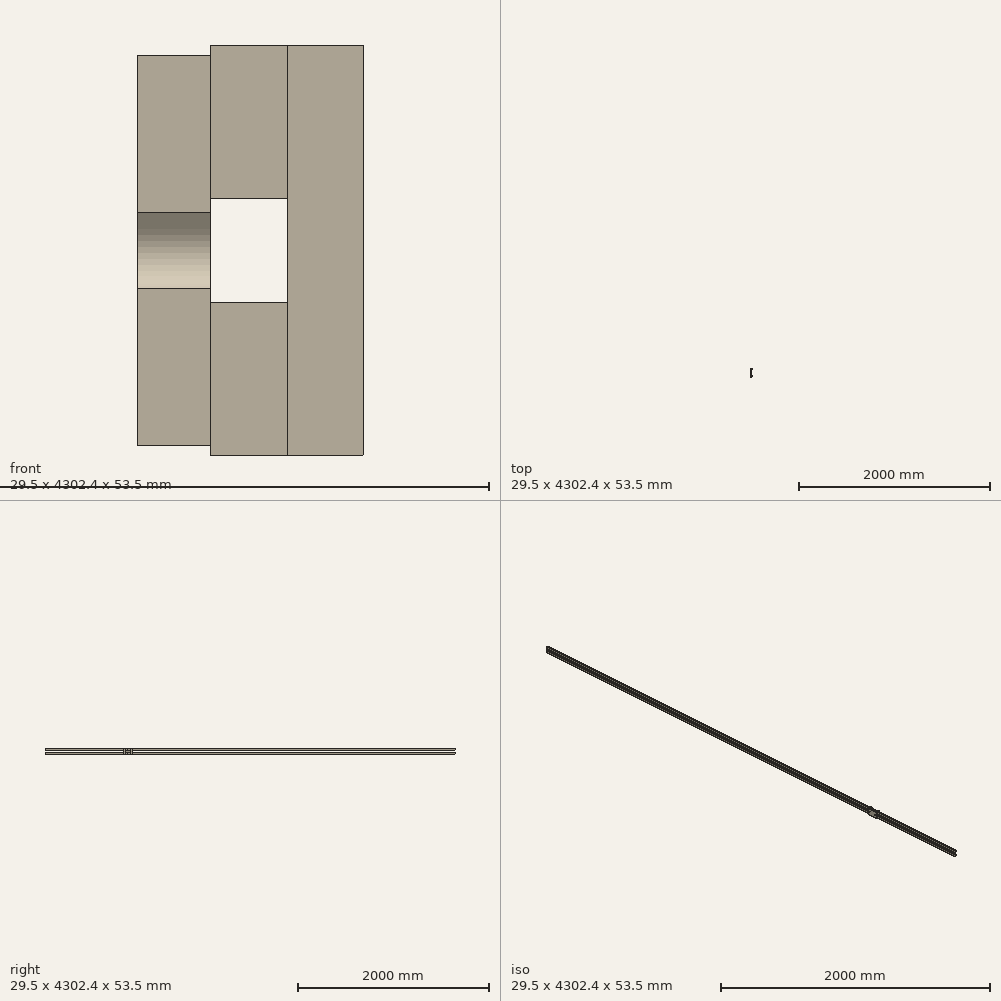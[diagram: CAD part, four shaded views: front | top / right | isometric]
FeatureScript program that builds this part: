
annotation { "Feature Type Name" : "Feature", "Feature Type Description" : "" }
export const myFeature = defineFeature(function(context is Context, id is Id, definition is map)
    precondition{}
    {
        {
            var Q0;
            Q0=qCreatedBy(makeId("Front.planeOp"),FACE);
            var sketch = newSketch(context, id + "F0", { "sketchPlane" : qUnion([Q0])});
            skLineSegment(sketch, "E0.bottom", {"start": v(-47.15, 37.14) * mm, "end": v(-37.15, 37.14) * mm});
            skLineSegment(sketch, "E0.top", {"start": v(-47.15, 17.14) * mm, "end": v(-37.15, 17.14) * mm});
            skLineSegment(sketch, "E0.left", {"start": v(-47.15, 37.14) * mm, "end": v(-47.15, 17.14) * mm});
            skLineSegment(sketch, "E0.right", {"start": v(-37.15, 37.14) * mm, "end": v(-37.15, 17.14) * mm});
            skLineSegment(sketch, "E1.bottom", {"start": v(-47.15, 3.67) * mm, "end": v(-37.15, 3.67) * mm});
            skLineSegment(sketch, "E1.top", {"start": v(-47.15, -16.33) * mm, "end": v(-37.15, -16.33) * mm});
            skLineSegment(sketch, "E1.left", {"start": v(-47.15, 3.67) * mm, "end": v(-47.15, -16.33) * mm});
            skLineSegment(sketch, "E1.right", {"start": v(-37.15, 3.67) * mm, "end": v(-37.15, -16.33) * mm});
            skPoint(sketch, "E2.startSnap0", {"position": v(-42.15, 37.14) * mm});
            skPoint(sketch, "E2.startSnap1", {"position": v(-47.15, 27.14) * mm});
            skPoint(sketch, "E2.endSnap0", {"position": v(-47.15, -6.33) * mm});
            skPoint(sketch, "E2.endSnap1", {"position": v(-42.15, 3.67) * mm});
            skSolve(sketch);
        }
        {
            var Q0;
            Q0=makeQuery(id+"F0.imprint","IMPRINT",FACE,{"disambiguationData":[TD([[makeQuery(id+"F0.imprint","IMPRINT",EDGE,{"derivedFrom":sQuery(id+"F0.wireOp",EDGE,"E0.bottom")}),-1.0]])]});
            var Q1;
            Q1=makeQuery(id+"F0.imprint","IMPRINT",FACE,{"disambiguationData":[TD([[makeQuery(id+"F0.imprint","IMPRINT",EDGE,{"derivedFrom":sQuery(id+"F0.wireOp",EDGE,"E1.bottom")}),-1.0]])]});
            extrude(context, id + "F1", {"entities" : qUnion([Q0, Q1]), "depth" : 4302.45 * mm});
        }
        {
            var Q0;
            Q0=makeQuery(id+"F1.opExtrude","SWEPT_FACE",FACE,{"disambiguationData":[OSD([sQuery(id+"F0.wireOp",EDGE,"E0.left")])]});
            var sketch = newSketch(context, id + "F2", { "sketchPlane" : qUnion([Q0])});
            skLineSegment(sketch, "E3.0.0", {"start": v(0, 3.67) * mm, "end": v(0, -16.33) * mm});
            skLineSegment(sketch, "E3.0.1", {"start": v(0, -16.33) * mm, "end": v(4302.45, -16.33) * mm});
            skLineSegment(sketch, "E3.0.2", {"start": v(4302.45, -16.33) * mm, "end": v(4302.45, 3.67) * mm});
            skLineSegment(sketch, "E3.0.3", {"start": v(4302.45, 3.67) * mm, "end": v(0, 3.67) * mm});
            skLineSegment(sketch, "E4", {"start": v(3483.33, 10.4) * mm, "end": v(3483.33, 35.8) * mm});
            skLineSegment(sketch, "E5", {"start": v(3483.33, 35.8) * mm, "end": v(3483.33, 10.4) * mm});
            skLineSegment(sketch, "E6", {"start": v(3483.33, 10.4) * mm, "end": v(3483.33, -15) * mm});
            skSolve(sketch);
        }
        {
            var Q0;
            Q0=sQuery(id+"F2.wireOp",EDGE,"E6");
            var Q1;
            Q1=sQuery(id+"F2.wireOp",EDGE,"E5");
            extrude(context, id + "F3", {"bodyType" : ToolBodyType.SURFACE, "surfaceEntities" : qUnion([Q0, Q1]), "depth" : 9.53 * mm, "offsetDistance" : 25 * mm});
        }
        {
            var Q0;
            Q0=makeQuery(id+"F3.opExtrude","SWEPT_FACE",FACE,{"disambiguationData":[OSD([sQuery(id+"F2.wireOp",EDGE,"E5"),sQuery(id+"F2.wireOp",EDGE,"E6")])]});
            extrude(context, id + "F4", {"entities" : qUnion([Q0]), "depth" : 90 * mm, "offsetDistance" : 25 * mm});
        }
        {
            var Q0;
            {var subQ0=sQuery(id+"F2.wireOp",EDGE,"E6");var subQ1=sQuery(id+"F2.wireOp",EDGE,"E5");Q0=makeQuery(id+"F4.opExtrude","SWEPT_FACE",FACE,{"disambiguationData":[OSD([subQ1,subQ0]),TDD([makeQuery(id+"F3.opExtrude","CAP_EDGE",EDGE,{"disambiguationData":[OSD([subQ1,subQ0])],"isStart":false})])]});}
            var sketch = newSketch(context, id + "F5", { "sketchPlane" : qUnion([Q0])});
            skLineSegment(sketch, "E7", {"start": v(3468.33, 5.4) * mm, "end": v(3483.33, 5.4) * mm});
            skLineSegment(sketch, "E8.MirrorCS", {"start": v(3468.33, 15.4) * mm, "end": v(3483.33, 15.4) * mm});
            skLineSegment(sketch, "E9", {"start": v(3468.33, 5.4) * mm, "end": v(3473.33, 5.4) * mm});
            skArc(sketch, "E10", {"start": v(3468.33, 15.4) * mm, "mid": v(3463.33, 10.4) * mm, "end": v(3468.33, 5.4) * mm});
            skSolve(sketch);
        }
        {
            var Q0;
            Q0=makeQuery(id+"F1.opExtrude","SWEPT_FACE",FACE,{"disambiguationData":[OSD([sQuery(id+"F0.wireOp",EDGE,"E1.right")])]});
            var sketch = newSketch(context, id + "F6", { "sketchPlane" : qUnion([Q0])});
            skLineSegment(sketch, "E11.0.0", {"start": v(-3483.33, 35.8) * mm, "end": v(-3483.33, 15.4) * mm});
            skLineSegment(sketch, "E11.0.4", {"start": v(-3483.33, 5.4) * mm, "end": v(-3483.33, -15) * mm});
            skLineSegment(sketch, "E11.0.6", {"start": v(-3393.33, -15) * mm, "end": v(-3393.33, 5.4) * mm});
            skLineSegment(sketch, "E11.0.10", {"start": v(-3393.33, 15.4) * mm, "end": v(-3393.33, 35.8) * mm});
            skLineSegment(sketch, "E12.0.1", {"start": v(0, 37.14) * mm, "end": v(-4302.45, 37.14) * mm});
            skLineSegment(sketch, "E13", {"start": v(-3483.33, 35.8) * mm, "end": v(-3483.33, 37.14) * mm});
            skLineSegment(sketch, "E14", {"start": v(-3483.33, 15.4) * mm, "end": v(-3483.33, 5.4) * mm});
            skLineSegment(sketch, "E15", {"start": v(-3483.33, -15) * mm, "end": v(-3483.33, -16.33) * mm});
            skLineSegment(sketch, "E16", {"start": v(-3483.33, -16.33) * mm, "end": v(-3463.33, -16.33) * mm});
            skLineSegment(sketch, "E17", {"start": v(-3463.33, -16.33) * mm, "end": v(-3463.33, 37.14) * mm});
            skLineSegment(sketch, "E18", {"start": v(-3463.33, 37.14) * mm, "end": v(-3483.33, 37.14) * mm});
            skLineSegment(sketch, "E19", {"start": v(-3393.33, 15.4) * mm, "end": v(-3393.33, 5.4) * mm});
            skLineSegment(sketch, "E20", {"start": v(-3393.33, 35.8) * mm, "end": v(-3393.33, 37.14) * mm});
            skLineSegment(sketch, "E21", {"start": v(-3393.33, 37.14) * mm, "end": v(-3413.33, 37.14) * mm});
            skLineSegment(sketch, "E22", {"start": v(-3413.33, 37.14) * mm, "end": v(-3413.33, -16.33) * mm});
            skLineSegment(sketch, "E23", {"start": v(-3413.33, -16.33) * mm, "end": v(-3393.33, -16.33) * mm});
            skLineSegment(sketch, "E24", {"start": v(-3393.33, -16.33) * mm, "end": v(-3393.33, -15) * mm});
            skSolve(sketch);
        }
        {
            var Q0;
            Q0=makeQuery(id+"F6.imprint","IMPRINT",FACE,{"disambiguationData":[TD([[makeQuery(id+"F6.imprint","IMPRINT",EDGE,{"derivedFrom":sQuery(id+"F6.wireOp",EDGE,"E11.0.0")}),1.0]])]});
            var Q1;
            {var subQ5=sQuery(id+"F6.wireOp",EDGE,"E15");Q1=makeQuery(id+"F6.imprint","IMPRINT",FACE,{"disambiguationData":[TD([[makeQuery(id+"F6.imprint","IMPRINT",EDGE,{"derivedFrom":subQ5}),1.0]])]});}
            var Q2;
            Q2=makeQuery(id+"F6.imprint","IMPRINT",FACE,{"disambiguationData":[TD([[makeQuery(id+"F6.imprint","IMPRINT",EDGE,{"derivedFrom":sQuery(id+"F6.wireOp",EDGE,"E11.0.10")}),1.0]])]});
            var Q3;
            {var subQ1=sQuery(id+"F6.wireOp",EDGE,"E23");Q3=makeQuery(id+"F6.imprint","IMPRINT",FACE,{"disambiguationData":[TD([[makeQuery(id+"F6.imprint","IMPRINT",EDGE,{"derivedFrom":subQ1}),1.0]])]});}
            extrude(context, id + "F7", {"entities" : qUnion([Q0, Q1, Q2, Q3]), "depth" : 10 * mm, "offsetDistance" : 25 * mm});
        }
        {
            var Q0;
            Q0=makeQuery(id+"F1.opExtrude","SWEPT_FACE",FACE,{"disambiguationData":[OSD([sQuery(id+"F0.wireOp",EDGE,"E0.bottom")])]});
            var sketch = newSketch(context, id + "F8", { "sketchPlane" : qUnion([Q0])});
            skLineSegment(sketch, "E25.0.0", {"start": v(-56.68, -3483.33) * mm, "end": v(-47.15, -3483.33) * mm});
            skLineSegment(sketch, "E25.0.1", {"start": v(-47.15, -3483.33) * mm, "end": v(-47.15, -3393.33) * mm});
            skLineSegment(sketch, "E25.0.2", {"start": v(-47.15, -3393.33) * mm, "end": v(-56.68, -3393.33) * mm});
            skLineSegment(sketch, "E25.0.3", {"start": v(-56.68, -3393.33) * mm, "end": v(-56.68, -3483.33) * mm});
            skLineSegment(sketch, "E26", {"start": v(-37.15, -3438.33) * mm, "end": v(-37.15, -3439.33) * mm});
            skLineSegment(sketch, "E27", {"start": v(-37.15, -3438.33) * mm, "end": v(-37.15, -3437.33) * mm});
            skLineSegment(sketch, "E28", {"start": v(-37.15, -3437.33) * mm, "end": v(-47.15, -3437.33) * mm});
            skLineSegment(sketch, "E29", {"start": v(-47.15, -3437.33) * mm, "end": v(-47.15, -3438.33) * mm});
            skLineSegment(sketch, "E30", {"start": v(-47.15, -3439.33) * mm, "end": v(-47.15, -3438.33) * mm});
            skLineSegment(sketch, "E31", {"start": v(-47.15, -3439.33) * mm, "end": v(-37.15, -3439.33) * mm});
            skSolve(sketch);
        }
        {
            var Q0;
            Q0=makeQuery(id+"F8.imprint","IMPRINT",FACE,{"disambiguationData":[TD([[makeQuery(id+"F8.imprint","IMPRINT",EDGE,{"derivedFrom":sQuery(id+"F8.wireOp",EDGE,"E26")}),1.0]])]});
            var Q1;
            Q1=makeQuery(id+"F1.opExtrude","SWEPT_FACE",FACE,{"disambiguationData":[OSD([sQuery(id+"F0.wireOp",EDGE,"E1.top")])]});
            extrude(context, id + "F9", {"entities" : qUnion([Q0]), "operationType" : NewBodyOperationType.REMOVE, "endBound" : BoundingType.UP_TO_SURFACE, "oppositeDirection" : true, "depth" : 25 * mm, "endBoundEntityFace" : qUnion([Q1]), "offsetDistance" : 25 * mm});
        }
        {
            var Q0;
            Q0=makeQuery(id+"F7.opExtrude","CAP_FACE",FACE,{"disambiguationData":[OSD([sQuery(id+"F6.wireOp",EDGE,"E11.0.0"),sQuery(id+"F6.wireOp",EDGE,"E11.0.4"),sQuery(id+"F6.wireOp",EDGE,"E12.0.1"),sQuery(id+"F6.wireOp",EDGE,"E13"),sQuery(id+"F6.wireOp",EDGE,"E14"),sQuery(id+"F6.wireOp",EDGE,"E15"),sQuery(id+"F6.wireOp",EDGE,"E16"),sQuery(id+"F6.wireOp",EDGE,"E17")])],"isStart":false});
            var sketch = newSketch(context, id + "F10", { "sketchPlane" : qUnion([Q0])});
            skCircle(sketch, "E32", {"center": v(-3473.33, 10.4) * mm, "radius": 5 * mm});
            skSolve(sketch);
        }
        {
            var Q0;
            Q0=makeQuery(id+"F7.opExtrude","CAP_FACE",FACE,{"disambiguationData":[OSD([sQuery(id+"F6.wireOp",EDGE,"E11.0.6"),sQuery(id+"F6.wireOp",EDGE,"E11.0.10"),sQuery(id+"F6.wireOp",EDGE,"E12.0.1"),sQuery(id+"F6.wireOp",EDGE,"E19"),sQuery(id+"F6.wireOp",EDGE,"E20"),sQuery(id+"F6.wireOp",EDGE,"E22"),sQuery(id+"F6.wireOp",EDGE,"E23"),sQuery(id+"F6.wireOp",EDGE,"E24")])],"isStart":false});
            var sketch = newSketch(context, id + "F11", { "sketchPlane" : qUnion([Q0])});
            skCircle(sketch, "E33", {"center": v(-3403.33, 10.4) * mm, "radius": 5 * mm});
            skSolve(sketch);
        }
        {
            var Q0;
            Q0=makeQuery(id+"F10.imprint","IMPRINT",FACE,{"disambiguationData":[TD([[makeQuery(id+"F10.imprint","IMPRINT",EDGE,{"derivedFrom":sQuery(id+"F10.wireOp",EDGE,"E32")}),1.0]])]});
            var Q1;
            Q1=makeQuery(id+"F11.imprint","IMPRINT",FACE,{"disambiguationData":[TD([[makeQuery(id+"F11.imprint","IMPRINT",EDGE,{"derivedFrom":sQuery(id+"F11.wireOp",EDGE,"E33")}),1.0]])]});
            extrude(context, id + "F12", {"entities" : qUnion([Q0, Q1]), "operationType" : NewBodyOperationType.REMOVE, "oppositeDirection" : true, "depth" : 10 * mm, "offsetDistance" : 25 * mm});
        }
        {
            var Q0;
            {var subQ1=sQuery(id+"F5.wireOp",EDGE,"E8.MirrorCS");Q0=makeQuery(id+"F5.imprint","IMPRINT",FACE,{"disambiguationData":[TD([[makeQuery(id+"F5.imprint","IMPRINT",EDGE,{"derivedFrom":subQ1}),1.0]])]});}
            var sketch = newSketch(context, id + "F13", { "sketchPlane" : qUnion([Q0])});
            skArc(sketch, "E34.0.0", {"start": v(3468.33, 5.4) * mm, "mid": v(3463.33, 10.4) * mm, "end": v(3468.33, 15.4) * mm});
            skLineSegment(sketch, "E34.0.1", {"start": v(3468.33, 15.4) * mm, "end": v(3483.33, 15.4) * mm});
            skLineSegment(sketch, "E34.0.2", {"start": v(3483.33, 15.4) * mm, "end": v(3483.33, 35.8) * mm});
            skLineSegment(sketch, "E34.0.3", {"start": v(3483.33, 35.8) * mm, "end": v(3393.33, 35.8) * mm});
            skLineSegment(sketch, "E34.0.4", {"start": v(3393.33, 35.8) * mm, "end": v(3393.33, -15) * mm});
            skLineSegment(sketch, "E34.0.5", {"start": v(3393.33, -15) * mm, "end": v(3483.33, -15) * mm});
            skLineSegment(sketch, "E34.0.6", {"start": v(3483.33, -15) * mm, "end": v(3483.33, 5.4) * mm});
            skLineSegment(sketch, "E34.0.7", {"start": v(3483.33, 5.4) * mm, "end": v(3473.33, 5.4) * mm});
            skLineSegment(sketch, "E34.0.8", {"start": v(3473.33, 5.4) * mm, "end": v(3468.33, 5.4) * mm});
            skLineSegment(sketch, "E35", {"start": v(3438.33, 35.8) * mm, "end": v(3438.33, -15) * mm});
            skLineSegment(sketch, "E36.MirrorCS", {"start": v(3393.33, 5.4) * mm, "end": v(3403.33, 5.4) * mm});
            skLineSegment(sketch, "E37.MirrorCS", {"start": v(3408.33, 15.4) * mm, "end": v(3393.33, 15.4) * mm});
            skLineSegment(sketch, "E38.MirrorCS", {"start": v(3403.33, 5.4) * mm, "end": v(3408.33, 5.4) * mm});
            skArc(sketch, "E39.MirrorCS", {"start": v(3408.33, 5.4) * mm, "mid": v(3413.33, 10.4) * mm, "end": v(3408.33, 15.4) * mm});
            skSolve(sketch);
        }
        {
            var Q0;
            {var subQ1=sQuery(id+"F13.wireOp",EDGE,"E36.MirrorCS");Q0=makeQuery(id+"F13.imprint","IMPRINT",FACE,{"disambiguationData":[TD([[makeQuery(id+"F13.imprint","IMPRINT",EDGE,{"derivedFrom":subQ1}),1.0]])]});}
            var Q1;
            {var subQ1=sQuery(id+"F5.wireOp",EDGE,"E8.MirrorCS");Q1=makeQuery(id+"F5.imprint","IMPRINT",FACE,{"disambiguationData":[TD([[makeQuery(id+"F5.imprint","IMPRINT",EDGE,{"derivedFrom":subQ1}),-1.0]])]});}
            var Q2;
            {var subQ0=sQuery(id+"F2.wireOp",EDGE,"E6");var subQ1=sQuery(id+"F2.wireOp",EDGE,"E5");Q2=makeQuery(id+"F4.opExtrude","SWEPT_FACE",FACE,{"disambiguationData":[OSD([subQ1,subQ0]),TDD([makeQuery(id+"F3.opExtrude","CAP_EDGE",EDGE,{"disambiguationData":[OSD([subQ1,subQ0])],"isStart":true})])]});}
            extrude(context, id + "F14", {"entities" : qUnion([Q0, Q1]), "operationType" : NewBodyOperationType.REMOVE, "endBound" : BoundingType.UP_TO_SURFACE, "oppositeDirection" : true, "depth" : 25 * mm, "endBoundEntityFace" : qUnion([Q2]), "offsetDistance" : 25 * mm});
        }
    });
